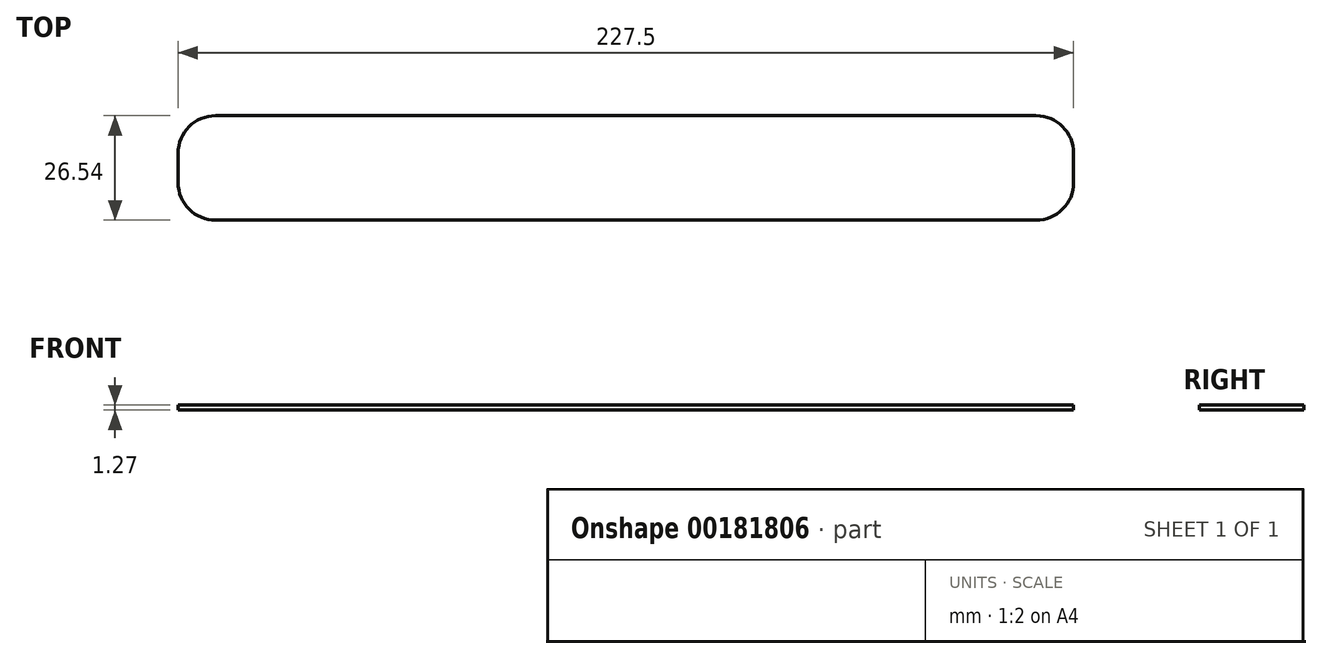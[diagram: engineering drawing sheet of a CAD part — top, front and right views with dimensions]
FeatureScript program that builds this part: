
annotation { "Feature Type Name" : "Feature", "Feature Type Description" : "" }
export const myFeature = defineFeature(function(context is Context, id is Id, definition is map)
    precondition{}
    {
        {
            var Q0;
            Q0=qCreatedBy(makeId("Top.planeOp"),FACE);
            var sketch = newSketch(context, id + "F0", { "sketchPlane" : qUnion([Q0])});
            skLineSegment(sketch, "E0.bottom", {"start": v(104.22, 13.27) * mm, "end": v(-104.22, 13.27) * mm});
            skLineSegment(sketch, "E0.top", {"start": v(104.22, -13.27) * mm, "end": v(-104.22, -13.27) * mm});
            skLineSegment(sketch, "E0.left", {"start": v(113.75, 3.75) * mm, "end": v(113.75, -3.75) * mm});
            skLineSegment(sketch, "E0.right", {"start": v(-113.75, 3.75) * mm, "end": v(-113.75, -3.75) * mm});
            skPoint(sketch, "E0.middle", {"position": v(0, 0) * mm});
            skPoint(sketch, "E1.visualSharp", {"position": v(-113.75, 13.27) * mm});
            skArc(sketch, "E1.filletArc", {"start": v(-104.22, 13.27) * mm, "mid": v(-110.96, 10.48) * mm, "end": v(-113.75, 3.75) * mm});
            skPoint(sketch, "E2.visualSharp", {"position": v(-113.75, -13.27) * mm});
            skArc(sketch, "E2.filletArc", {"start": v(-113.75, -3.75) * mm, "mid": v(-110.96, -10.48) * mm, "end": v(-104.22, -13.27) * mm});
            skPoint(sketch, "E3.visualSharp", {"position": v(113.75, 13.27) * mm});
            skArc(sketch, "E3.filletArc", {"start": v(113.75, 3.75) * mm, "mid": v(110.96, 10.48) * mm, "end": v(104.22, 13.27) * mm});
            skPoint(sketch, "E4.visualSharp", {"position": v(113.75, -13.27) * mm});
            skArc(sketch, "E4.filletArc", {"start": v(104.22, -13.27) * mm, "mid": v(110.96, -10.48) * mm, "end": v(113.75, -3.75) * mm});
            skSolve(sketch);
        }
        {
            var Q0;
            Q0 = qSketchRegion(id + "F0", true);
            extrude(context, id + "F1", {"entities" : qUnion([Q0]), "oppositeDirection" : true, "depth" : 1.27 * mm});
        }
    });
